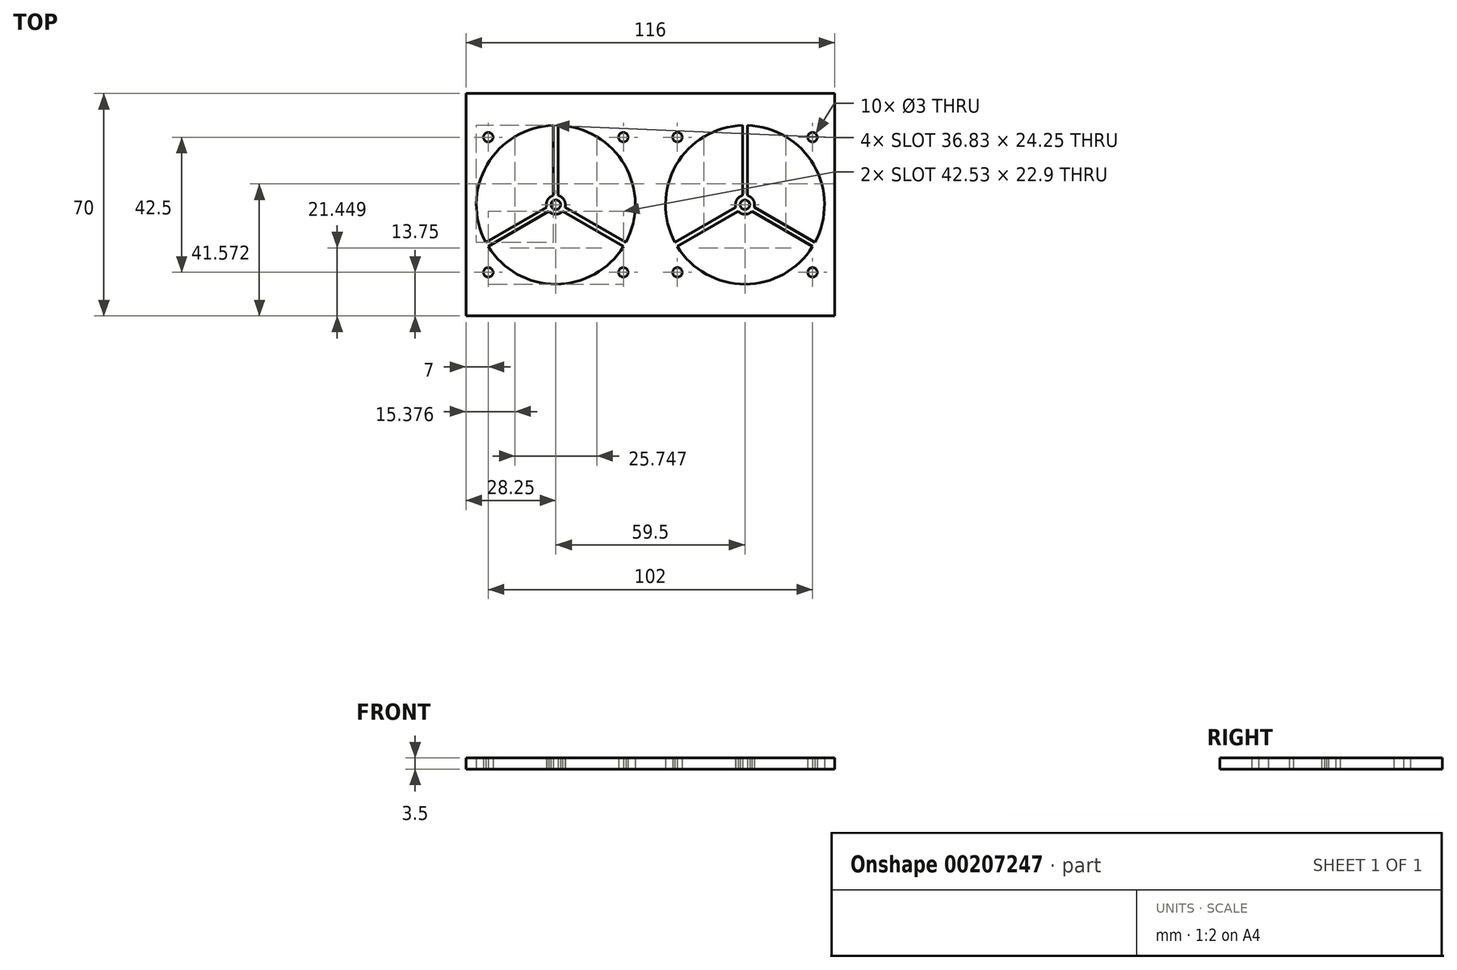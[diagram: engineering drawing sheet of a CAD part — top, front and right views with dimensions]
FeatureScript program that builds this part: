
annotation { "Feature Type Name" : "Feature", "Feature Type Description" : "" }
export const myFeature = defineFeature(function(context is Context, id is Id, definition is map)
    precondition{}
    {
        {
            var Q0;
            Q0=qCreatedBy(makeId("Top.planeOp"),FACE);
            var sketch = newSketch(context, id + "F0", { "sketchPlane" : qUnion([Q0])});
            skLineSegment(sketch, "E0", {"start": v(-29.75, 0) * mm, "end": v(0, 0) * mm, "construction": true});
            skLineSegment(sketch, "E1", {"start": v(29.75, 0) * mm, "end": v(0, 0) * mm, "construction": true});
            skLineSegment(sketch, "E2", {"start": v(-67.56, 21.25) * mm, "end": v(64.22, 21.25) * mm, "construction": true});
            skLineSegment(sketch, "E3", {"start": v(65.43, -21.25) * mm, "end": v(-81.7, -21.25) * mm, "construction": true});
            skLineSegment(sketch, "E4", {"start": v(-8.5, 39.08) * mm, "end": v(-8.5, -41.36) * mm, "construction": true});
            skLineSegment(sketch, "E5", {"start": v(-51, 34.84) * mm, "end": v(-51, -39.94) * mm, "construction": true});
            skLineSegment(sketch, "E6.bottom", {"start": v(-58, -35) * mm, "end": v(58, -35) * mm});
            skLineSegment(sketch, "E6.top", {"start": v(-58, 35) * mm, "end": v(58, 35) * mm});
            skLineSegment(sketch, "E6.left", {"start": v(-58, -35) * mm, "end": v(-58, 35) * mm});
            skLineSegment(sketch, "E6.right", {"start": v(58, -35) * mm, "end": v(58, 35) * mm});
            skLineSegment(sketch, "E7", {"start": v(0, 39.29) * mm, "end": v(0, -41.56) * mm, "construction": true});
            skPoint(sketch, "E8", {"position": v(-51, 21.25) * mm});
            skPoint(sketch, "E9", {"position": v(-8.5, 21.25) * mm});
            skPoint(sketch, "E10", {"position": v(-8.5, -21.25) * mm});
            skPoint(sketch, "E11", {"position": v(-51, -21.25) * mm});
            skPoint(sketch, "E12.MirrorP", {"position": v(8.5, 21.25) * mm});
            skPoint(sketch, "E13.MirrorP", {"position": v(51, 21.25) * mm});
            skPoint(sketch, "E14.MirrorP", {"position": v(51, -21.25) * mm});
            skPoint(sketch, "E15.MirrorP", {"position": v(8.5, -21.25) * mm});
            skLineSegment(sketch, "E16", {"start": v(-58, 29.55) * mm, "end": v(-58, 44.03) * mm, "construction": true});
            skLineSegment(sketch, "E17", {"start": v(-58, 40.48) * mm, "end": v(0, 40.48) * mm, "construction": true});
            skLineSegment(sketch, "E18", {"start": v(58, 40.48) * mm, "end": v(0, 40.48) * mm, "construction": true});
            skPoint(sketch, "E19.center", {"position": v(-29.75, 0) * mm});
            skPoint(sketch, "E20.center", {"position": v(29.75, 0) * mm});
            skArc(sketch, "E21", {"start": v(-30.5, 24.99) * mm, "mid": v(-51.4, 12.5) * mm, "end": v(-51.77, -11.84) * mm});
            skCircle(sketch, "E22", {"center": v(-29.75, 0) * mm, "radius": 1.5 * mm});
            skArc(sketch, "E23", {"start": v(-30.5, 2.9) * mm, "mid": v(-32.35, 1.5) * mm, "end": v(-32.64, -0.8) * mm});
            skLineSegment(sketch, "E24.left", {"start": v(-29, 24.99) * mm, "end": v(-29, 2.9) * mm});
            skLineSegment(sketch, "E24.right", {"start": v(-30.5, 24.99) * mm, "end": v(-30.5, 2.9) * mm});
            skPoint(sketch, "E24.middle", {"position": v(-29.75, 14.1) * mm});
            skLineSegment(sketch, "E25.1.0", {"start": v(-51.02, -13.14) * mm, "end": v(-31.9, -2.1) * mm});
            skLineSegment(sketch, "E25.1.1", {"start": v(-51.77, -11.84) * mm, "end": v(-32.64, -0.8) * mm});
            skLineSegment(sketch, "E25.2.0", {"start": v(-7.73, -11.84) * mm, "end": v(-26.86, -0.8) * mm});
            skLineSegment(sketch, "E25.2.1", {"start": v(-8.48, -13.14) * mm, "end": v(-27.6, -2.1) * mm});
            skArc(sketch, "E26.trimOffspring", {"start": v(-31.9, -2.1) * mm, "mid": v(-29.75, -3) * mm, "end": v(-27.6, -2.1) * mm});
            skArc(sketch, "E27.trimOffspring", {"start": v(-26.86, -0.8) * mm, "mid": v(-27.15, 1.5) * mm, "end": v(-29, 2.9) * mm});
            skArc(sketch, "E28.trimOffspring", {"start": v(-7.73, -11.84) * mm, "mid": v(-8.1, 12.5) * mm, "end": v(-29, 24.99) * mm});
            skLineSegment(sketch, "E29.MirrorCS", {"start": v(30.5, 24.99) * mm, "end": v(30.5, 2.9) * mm});
            skLineSegment(sketch, "E30.MirrorCS", {"start": v(29, 24.99) * mm, "end": v(29, 2.9) * mm});
            skLineSegment(sketch, "E31.MirrorCS", {"start": v(51.77, -11.84) * mm, "end": v(32.64, -0.8) * mm});
            skLineSegment(sketch, "E32.MirrorCS", {"start": v(51.02, -13.14) * mm, "end": v(31.9, -2.1) * mm});
            skLineSegment(sketch, "E33.MirrorCS", {"start": v(8.48, -13.14) * mm, "end": v(27.6, -2.1) * mm});
            skLineSegment(sketch, "E34.MirrorCS", {"start": v(7.73, -11.84) * mm, "end": v(26.86, -0.8) * mm});
            skArc(sketch, "E35.MirrorCS", {"start": v(26.86, -0.8) * mm, "mid": v(27.15, 1.5) * mm, "end": v(29, 2.9) * mm});
            skArc(sketch, "E36.MirrorCS", {"start": v(31.9, -2.1) * mm, "mid": v(29.75, -3) * mm, "end": v(27.6, -2.1) * mm});
            skArc(sketch, "E37.MirrorCS", {"start": v(30.5, 2.9) * mm, "mid": v(32.35, 1.5) * mm, "end": v(32.64, -0.8) * mm});
            skCircle(sketch, "E38.MirrorC", {"center": v(29.75, 0) * mm, "radius": 1.5 * mm});
            skArc(sketch, "E39.MirrorCS", {"start": v(7.73, -11.84) * mm, "mid": v(8.1, 12.5) * mm, "end": v(29, 24.99) * mm});
            skArc(sketch, "E40.MirrorCS", {"start": v(30.5, 24.99) * mm, "mid": v(51.4, 12.5) * mm, "end": v(51.77, -11.84) * mm});
            skArc(sketch, "E41.trimOffspring", {"start": v(-51.02, -13.14) * mm, "mid": v(-29.75, -25) * mm, "end": v(-8.48, -13.14) * mm});
            skArc(sketch, "E42.trimOffspring", {"start": v(51.02, -13.14) * mm, "mid": v(29.75, -25) * mm, "end": v(8.48, -13.14) * mm});
            skSolve(sketch);
        }
        {
            var Q0;
            Q0=makeQuery(id+"F0.imprint","IMPRINT",FACE,{"disambiguationData":[TD([[makeQuery(id+"F0.imprint","IMPRINT",EDGE,{"derivedFrom":sQuery(id+"F0.wireOp",EDGE,"0BlL0anx-IE55-3Ffi-SPci-i4BzROD0rsbx")}),-1.0]])]});
            var Q1;
            {var subQ3=sQuery(id+"F0.wireOp",EDGE,"E6.bottom");Q1=makeQuery(id+"F0.imprint","IMPRINT",FACE,{"disambiguationData":[TD([[makeQuery(id+"F0.imprint","IMPRINT",EDGE,{"derivedFrom":subQ3}),1.0]])]});}
            extrude(context, id + "F1", {"entities" : qUnion([Q0, Q1]), "depth" : 3.5 * mm});
        }
        {
            var Q0;
            Q0=sQuery(id+"F0.wireOp",VERTEX,"E8");
            var Q1;
            Q1=sQuery(id+"F0.wireOp",VERTEX,"E11");
            var Q2;
            Q2=sQuery(id+"F0.wireOp",VERTEX,"E10");
            var Q3;
            Q3=sQuery(id+"F0.wireOp",VERTEX,"E9");
            var Q4;
            Q4=sQuery(id+"F0.wireOp",VERTEX,"E12.MirrorP");
            var Q5;
            Q5=sQuery(id+"F0.wireOp",VERTEX,"E15.MirrorP");
            var Q6;
            Q6=sQuery(id+"F0.wireOp",VERTEX,"E14.MirrorP");
            var Q7;
            Q7=sQuery(id+"F0.wireOp",VERTEX,"E13.MirrorP");
            var Q8;
            Q8=makeQuery(id+"F1.opExtrude","SWEPT_BODY",BODY,{"disambiguationData":[OSD([sQuery(id+"F0.wireOp",EDGE,"0BlL0anx-IE55-3Ffi-SPci-i4BzROD0rsbx"),sQuery(id+"F0.wireOp",EDGE,"11NtaD0y-CNwM-gsSJ-spU2-3III16kJOtdG"),sQuery(id+"F0.wireOp",EDGE,"E6.bottom"),sQuery(id+"F0.wireOp",EDGE,"E6.top"),sQuery(id+"F0.wireOp",EDGE,"E6.left"),sQuery(id+"F0.wireOp",EDGE,"E6.right")])]});
            hole(context, id + "F2", {"style" : HoleStyle.SIMPLE, "endStyle" : HoleEndStyle.THROUGH, "oppositeDirection" : true, "holeDiameter" : 3 * mm, "startFromSketch" : true, "locations" : qUnion([Q0, Q1, Q2, Q3, Q4, Q5, Q6, Q7]), "scope" : qUnion([Q8]), "isTappedThrough" : true});
        }
    });
